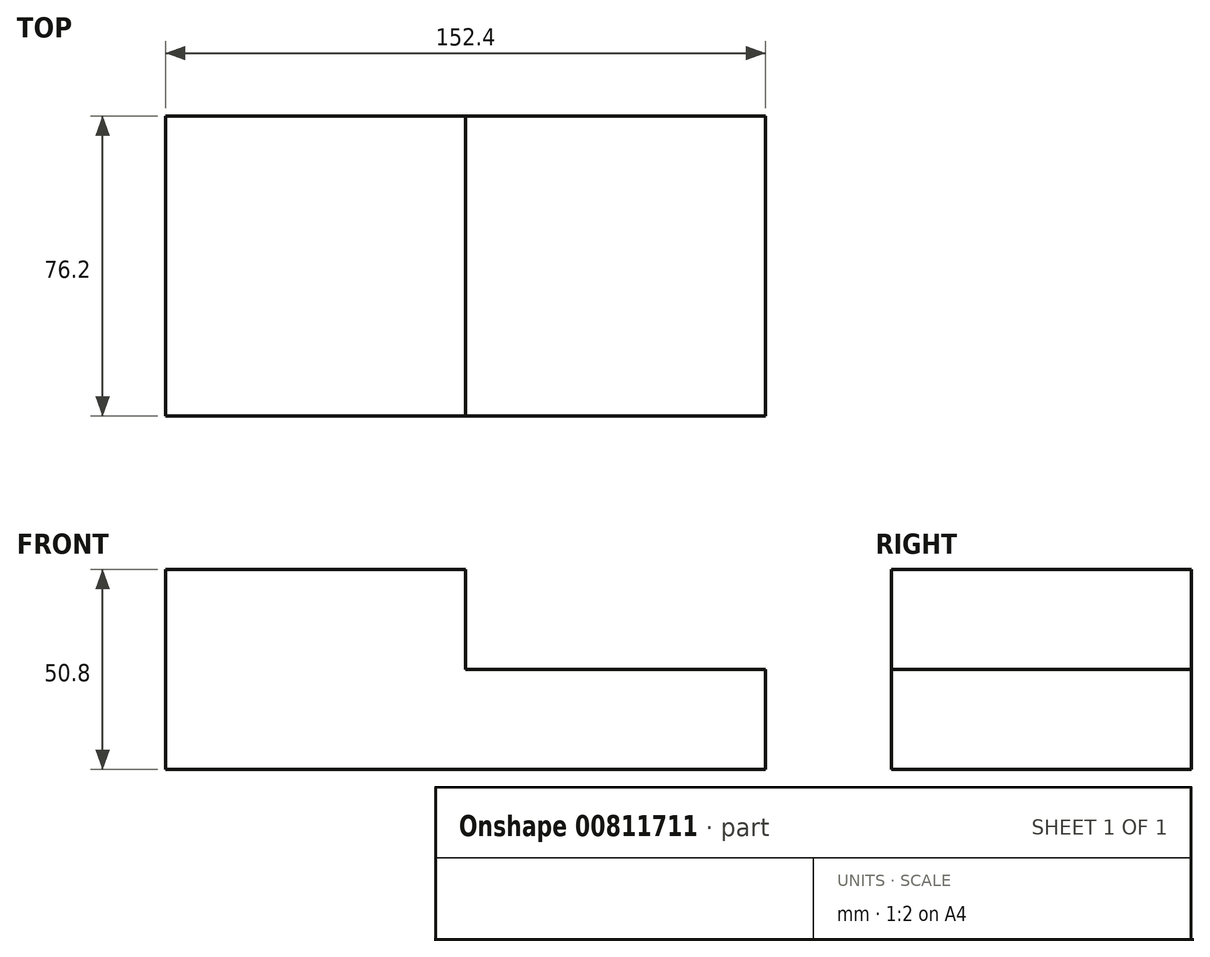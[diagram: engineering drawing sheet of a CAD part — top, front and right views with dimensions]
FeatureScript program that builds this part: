
annotation { "Feature Type Name" : "Feature", "Feature Type Description" : "" }
export const myFeature = defineFeature(function(context is Context, id is Id, definition is map)
    precondition{}
    {
        {
            var Q0;
            Q0=qCreatedBy(makeId("Front.planeOp"),FACE);
            var sketch = newSketch(context, id + "F0", { "sketchPlane" : qUnion([Q0])});
            skLineSegment(sketch, "E0", {"start": v(0, 0) * mm, "end": v(152.4, 0) * mm});
            skLineSegment(sketch, "E1", {"start": v(152.4, 0) * mm, "end": v(152.4, 25.4) * mm});
            skLineSegment(sketch, "E2", {"start": v(152.4, 25.4) * mm, "end": v(76.2, 25.4) * mm});
            skLineSegment(sketch, "E3", {"start": v(76.2, 25.4) * mm, "end": v(76.2, 50.8) * mm});
            skLineSegment(sketch, "E4", {"start": v(76.2, 50.8) * mm, "end": v(0, 50.8) * mm});
            skLineSegment(sketch, "E5", {"start": v(0, 50.8) * mm, "end": v(0, 0) * mm});
            skSolve(sketch);
        }
        {
            var Q0;
            Q0 = qSketchRegion(id + "F0", true);
            extrude(context, id + "F1", {"entities" : qUnion([Q0]), "depth" : 76.2 * mm, "offsetDistance" : 25.4 * mm});
        }
    });
